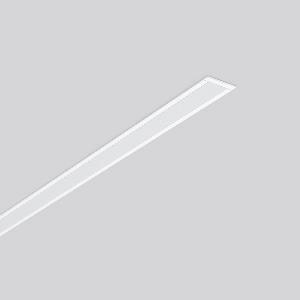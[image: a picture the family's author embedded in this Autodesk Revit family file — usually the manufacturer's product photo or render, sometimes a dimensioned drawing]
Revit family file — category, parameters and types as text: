
# Revit family: less_is_more_27_312178_002_1_76_c11b
name_source: partatom
category: Lighting Fixtures
units: mm (PartAtom-declared; Revit-internal decimal feet)

## family parameters
Cut with Voids When Loaded = No
Host = Face
Light Source = No
Part Type = Normal
Room Calculation Point = No
Round Connector Dimension = Use Diameter
Shared = No

## types (1)
- LESS IS MORE 27 (1 x LED Modul 840, 2900 lm, 4000)
    Apparent Load = 39 VA
    CIE Flux Codes = 48 79 96 100 100
    Color Rendering = 80
    Color Temperature = 4000
    Default Elevation = 1800 mm
    Description = Series: LESS IS MORE 27
Recessed ceiling and wall luminaire with slim design. Housing: extruded aluminium profile, powder-coated. End cap aluminium powder-coated. Diffuser made of non-yellowing plastic (PMMA), opal. Suitable for Recessed ceiling mounting, wall (recessed). External driver with connecting cable. 
Colour: traffic white, matt (RAL 9016)
Length: 1514 mm
Width: 38 mm
Height: 2 mm
Cut-out length: 1506 mm
Cut-out width: 30 mm
Recess height: 45-60 mm
Luminaire: recess height: 37 mm
Lamp: LED
Socket: without socket
Colour temperature: 4000K
Colour rendering index (CRI): 82
System power: 39 W
Rated luminous flux: 2900 lm
Luminous efficiency: 74 lm/W
Control gear: Voltage converter, DALI dim.
Protection class: II
Type of protection: IP 20
    Height = 0 mm  [stored 0 ft]
    Lamp = 1 x LED Modul 840
    Lamp Light Flux = 2900 lm
    Lamp count = 1
    Length = 1514 mm
    Lifetime = 50000 h
    Luminous efficacy = 74 lm/W
    Manufacturer = RZB
    ModVariant = No
    Model = 312178.002.1.76
    Mounting Place = Ceiling, Wall
    Mounting Type = Recessed
    Number of Poles = 1
    OnlyDefault = Yes
    Power Factor = 1
    Product Name = LESS IS MORE 27
    Product group = Recessed LED linear luminaires
    ProductGroupID = 407
    Protection Class = Protection class II
    Protection Degree = IP 20
    RLX_Detail_Level = 1
    RLX_Emergency_Light_Flux = 0 lm
    RLX_Emergency_Type = 0
    RLX_Emergency_Type_DB = No
    RlxData = <blob elided: 21589 chars, md5=755af8bb>
    Socket = socket
    Standby Power = 0 W
    System Light Flux = 2900 lm
    System Power = 39 W
    Type Comments = Product without accessories
    Type Image = 312176.002.jpg
    URL = http://relux.com
    VarID = ---
    Voltage = 230 V
    Voltage Range = 220-240 V
    Weight = 0.00 kg
    Width = 38 mm

note: [stored X ft] marks values corroborated as IEEE doubles in the binary element streams (Revit-internal decimal feet)

## geometry (parser evidence)
native form markers: Blend x4, Sweep x10
no freeform markers — native parametric forms only
